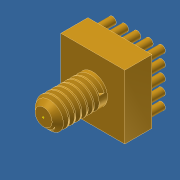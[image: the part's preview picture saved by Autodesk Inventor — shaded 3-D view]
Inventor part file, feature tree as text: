
AUTODESK INVENTOR PART (.ipt)
format: ipt  version: 2012 (Build 160160000, 160)  size: 232,448 bytes
history: native  units: mm (DEFAULTED — no unit token found)
features: sketch x5, extrude x3, chamfer x1, helix x1
ambient origin geometry x8: Origin, YZ Plane, XZ Plane, XY Plane, X Axis, Y Axis, Z Axis, Center Point
bodies: Solid1 (feature_tree)
feature tree (10):
  extrude  "Extrusion1"  Depth=13.0mm
  extrude  "Extrusion2"  Depth=5.95mm
  chamfer  "Chamfer1"  Distance=10.0mm
  helix  "Coil1"  [1 undecoded]
  extrude  "Extrusion3"  Depth=6.0mm
  sketch  "Sketch5"  dims[d20=50.0mm d22=2.5mm d23=50.0mm d25=2.5mm d28=1.5mm d29=3.5mm d30=0.0mm]
  sketch  "Sketch1"  dims[d0=13.0mm d1=13.0mm]
  sketch  "Sketch2"  dims[d2=5.5mm d3=0.0mm d4=5.95mm d5=10.0mm d6=0.0mm d7=1.25mm d8=2.0mm d9=45.0deg]
  sketch  "Sketch3"  dims[d10=1.0mm d11=6.0mm]
  sketch  "Sketch4"  dims[d12=1.25mm d13=9.0mm d14=10.0mm d15=0.0mm d16=90.0deg d17=90.0deg d18=0.0mm d19=0.0mm]
note: 1 required parameter value undecoded (feature->parameter linkage not recoverable at this tier; creation-order binding heuristic only, values carry confidence <= 0.55)
